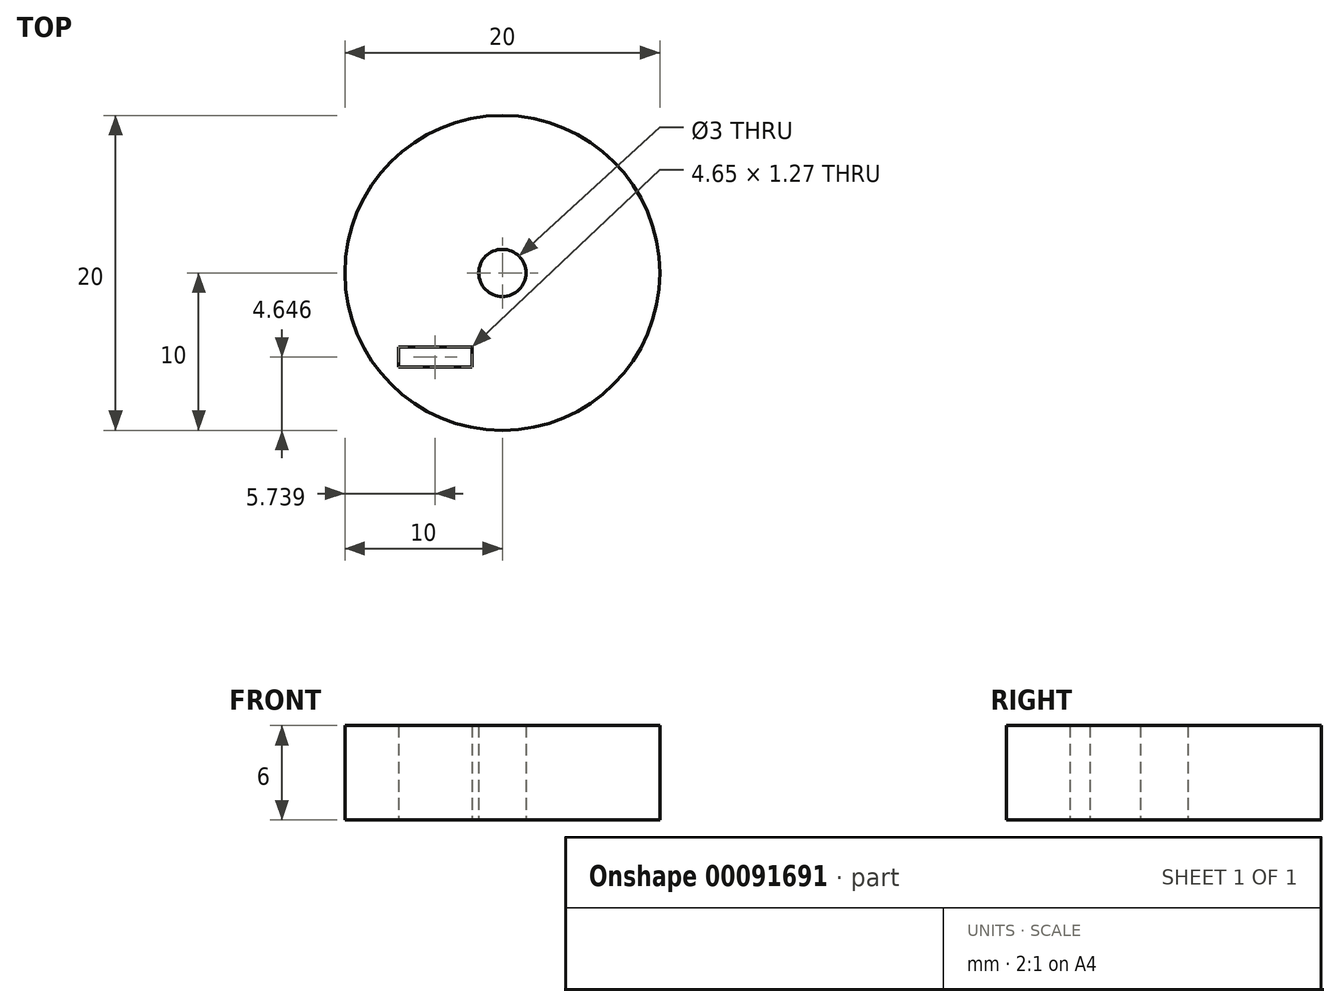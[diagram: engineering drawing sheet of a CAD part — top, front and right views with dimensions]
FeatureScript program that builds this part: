
annotation { "Feature Type Name" : "Feature", "Feature Type Description" : "" }
export const myFeature = defineFeature(function(context is Context, id is Id, definition is map)
    precondition{}
    {
        {
            var Q0;
            Q0=qCreatedBy(makeId("Top.planeOp"),FACE);
            var sketch = newSketch(context, id + "F0", { "sketchPlane" : qUnion([Q0])});
            skCircle(sketch, "E0", {"center": v(0, 0) * mm, "radius": 10 * mm});
            skCircle(sketch, "E1", {"center": v(0, 0) * mm, "radius": 1.5 * mm});
            skLineSegment(sketch, "E2.bottom", {"start": v(-6.58, -4.72) * mm, "end": v(-1.94, -4.72) * mm});
            skLineSegment(sketch, "E2.top", {"start": v(-6.58, -5.99) * mm, "end": v(-1.94, -5.99) * mm});
            skLineSegment(sketch, "E2.left", {"start": v(-6.58, -4.72) * mm, "end": v(-6.58, -5.99) * mm});
            skLineSegment(sketch, "E2.right", {"start": v(-1.94, -4.72) * mm, "end": v(-1.94, -5.99) * mm});
            skSolve(sketch);
        }
        {
            var Q0;
            Q0=makeQuery(id+"F0.imprint","IMPRINT",FACE,{"disambiguationData":[TD([[makeQuery(id+"F0.imprint","IMPRINT",EDGE,{"derivedFrom":sQuery(id+"F0.wireOp",EDGE,"E0")}),1.0]])]});
            extrude(context, id + "F1", {"entities" : qUnion([Q0]), "depth" : 6 * mm});
        }
    });
